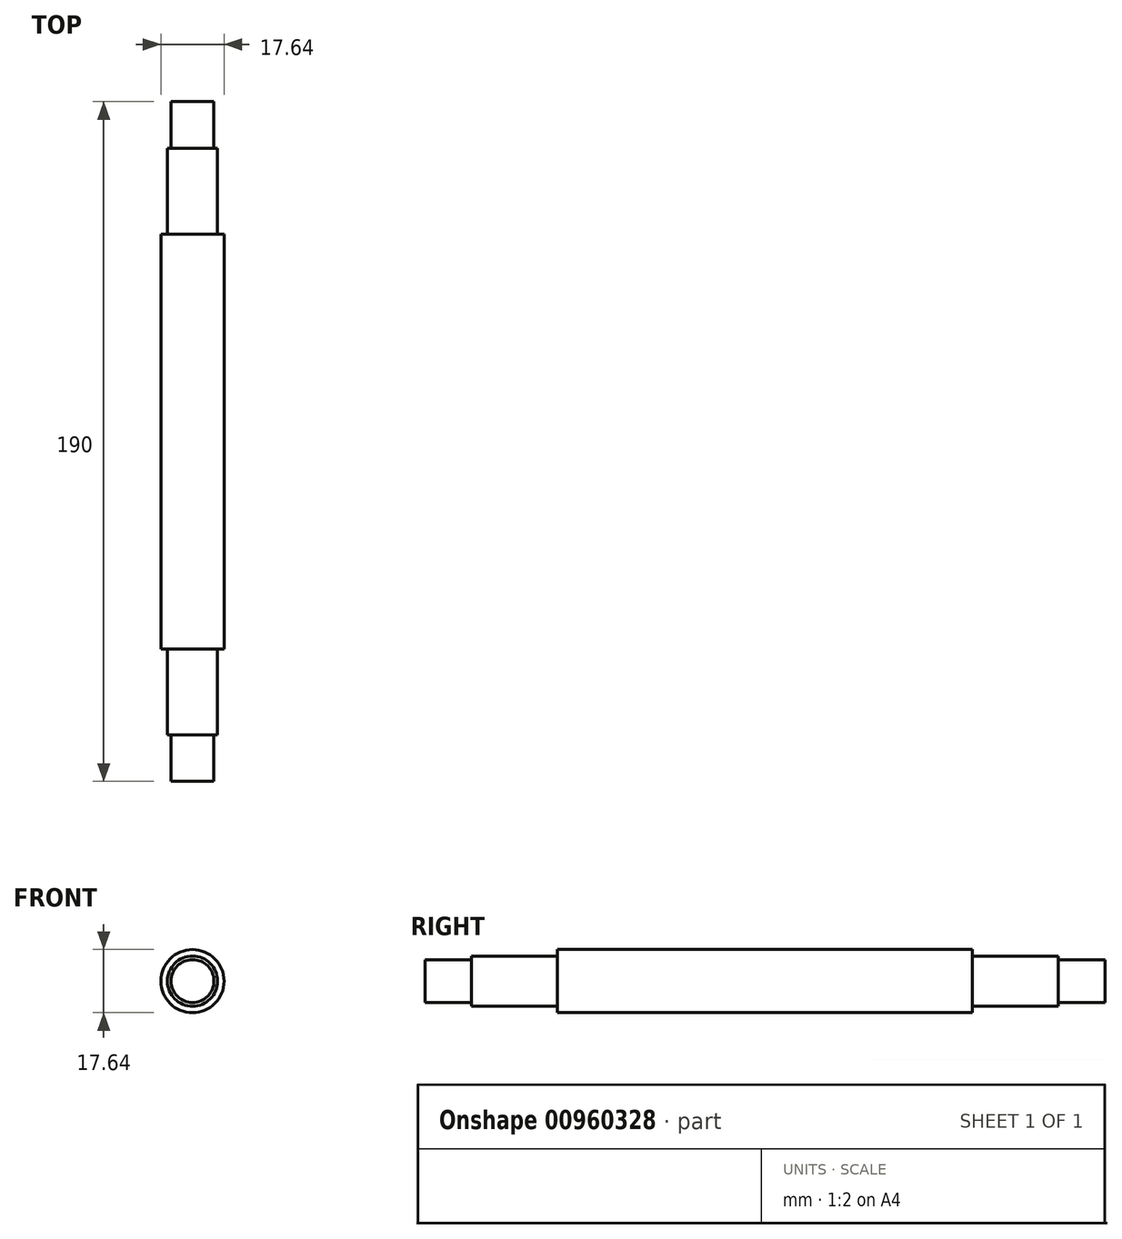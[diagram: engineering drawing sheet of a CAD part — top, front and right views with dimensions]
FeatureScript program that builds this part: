
annotation { "Feature Type Name" : "Feature", "Feature Type Description" : "" }
export const myFeature = defineFeature(function(context is Context, id is Id, definition is map)
    precondition{}
    {
        {
            var Q0;
            Q0=qCreatedBy(makeId("Right.planeOp"),FACE);
            var sketch = newSketch(context, id + "F0", { "sketchPlane" : qUnion([Q0])});
            skLineSegment(sketch, "E0", {"start": v(-39.95, 0) * mm, "end": v(170.07, 0) * mm, "construction": true});
            skLineSegment(sketch, "E1", {"start": v(-33.23, 0) * mm, "end": v(-33.23, 6) * mm});
            skLineSegment(sketch, "E2", {"start": v(-33.23, 6) * mm, "end": v(-20.23, 6) * mm});
            skLineSegment(sketch, "E3", {"start": v(-20.23, 6) * mm, "end": v(-20.23, 7) * mm});
            skLineSegment(sketch, "E4", {"start": v(-20.23, 7) * mm, "end": v(3.77, 7) * mm});
            skLineSegment(sketch, "E5", {"start": v(3.77, 7) * mm, "end": v(3.77, 8.82) * mm});
            skLineSegment(sketch, "E6", {"start": v(3.77, 8.82) * mm, "end": v(119.77, 8.82) * mm});
            skLineSegment(sketch, "E7", {"start": v(119.77, 8.82) * mm, "end": v(119.77, 7) * mm});
            skLineSegment(sketch, "E8", {"start": v(119.77, 7) * mm, "end": v(143.77, 7) * mm});
            skLineSegment(sketch, "E9", {"start": v(143.77, 7) * mm, "end": v(143.77, 6) * mm});
            skLineSegment(sketch, "E10", {"start": v(143.77, 6) * mm, "end": v(156.77, 6) * mm});
            skLineSegment(sketch, "E11", {"start": v(156.77, 6) * mm, "end": v(156.77, 0) * mm});
            skLineSegment(sketch, "E12", {"start": v(156.77, 0) * mm, "end": v(-33.23, 0) * mm});
            skSolve(sketch);
        }
        {
            var Q0;
            Q0=makeQuery(id+"F0.imprint","IMPRINT",FACE,{"disambiguationData":[TD([[makeQuery(id+"F0.imprint","IMPRINT",EDGE,{"derivedFrom":sQuery(id+"F0.wireOp",EDGE,"E1")}),-1.0]])]});
            var Q1;
            Q1=sQuery(id+"F0.wireOp",EDGE,"E12");
            revolve(context, id + "F1", {"surfaceOperationType" : NewSurfaceOperationType.NEW, "entities" : qUnion([Q0]), "axis" : qUnion([Q1]), "revolveType" : RevolveType.FULL});
        }
    });
